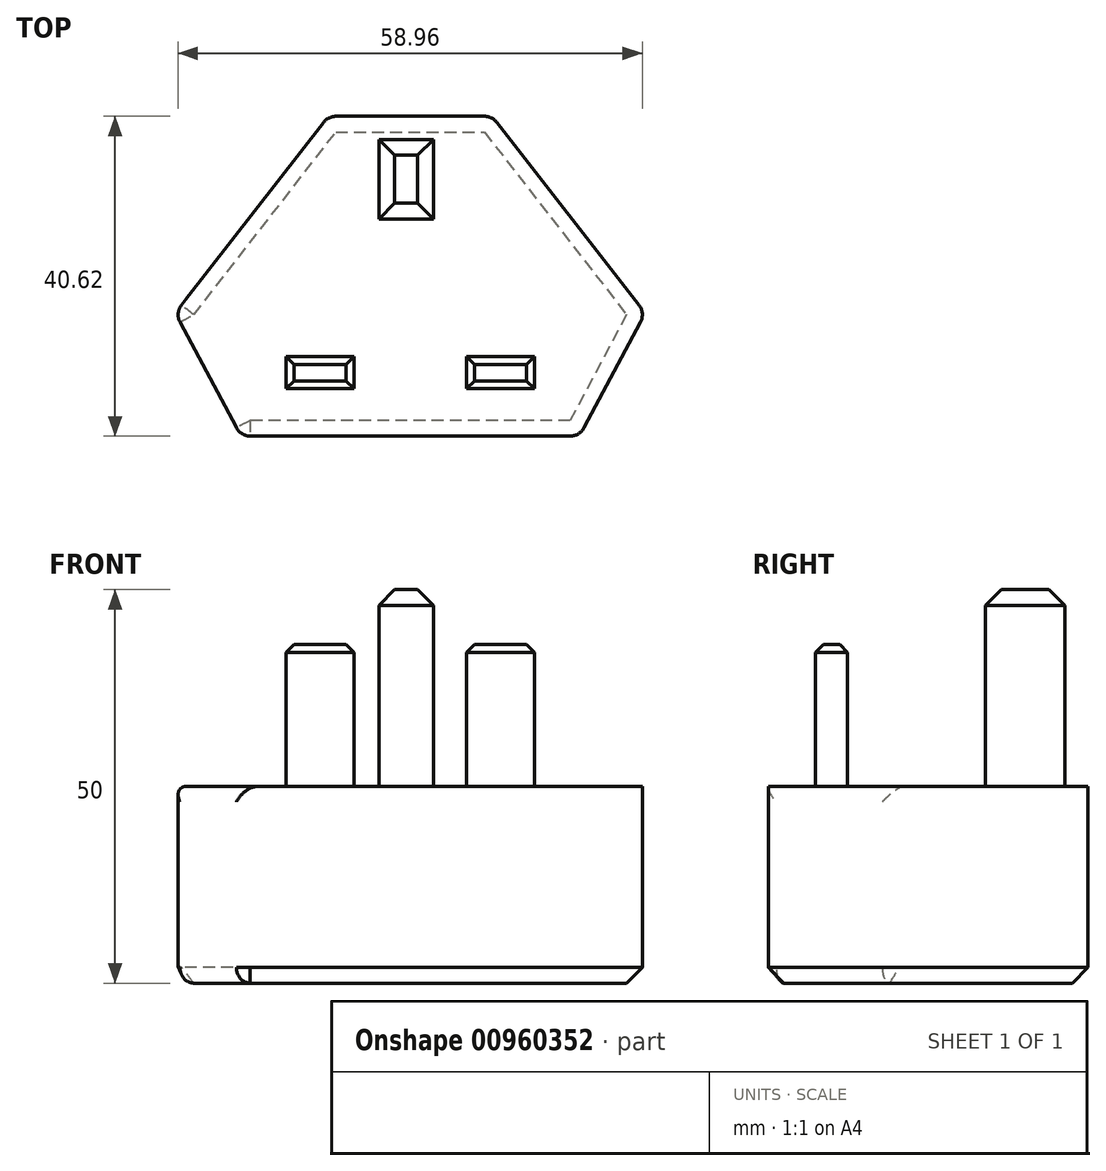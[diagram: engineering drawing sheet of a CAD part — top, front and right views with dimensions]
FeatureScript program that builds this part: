
annotation { "Feature Type Name" : "Feature", "Feature Type Description" : "" }
export const myFeature = defineFeature(function(context is Context, id is Id, definition is map)
    precondition{}
    {
        {
            var Q0;
            Q0=qCreatedBy(makeId("Top.planeOp"),FACE);
            var sketch = newSketch(context, id + "F0", { "sketchPlane" : qUnion([Q0])});
            skLineSegment(sketch, "E0", {"start": v(0, 21.7) * mm, "end": v(10.42, 21.7) * mm});
            skLineSegment(sketch, "E1", {"start": v(10.42, 21.7) * mm, "end": v(29.86, -3.3) * mm});
            skLineSegment(sketch, "E2", {"start": v(29.86, -3.3) * mm, "end": v(21.52, -18.92) * mm});
            skLineSegment(sketch, "E3", {"start": v(21.52, -18.92) * mm, "end": v(0, -18.92) * mm});
            skLineSegment(sketch, "E4", {"start": v(0, 40.44) * mm, "end": v(0, -43.92) * mm, "construction": true});
            skLineSegment(sketch, "E5.MirrorCS", {"start": v(-10.42, 21.7) * mm, "end": v(-29.86, -3.3) * mm});
            skLineSegment(sketch, "E6.MirrorCS", {"start": v(0, 21.7) * mm, "end": v(-10.42, 21.7) * mm});
            skLineSegment(sketch, "E7.MirrorCS", {"start": v(-29.86, -3.3) * mm, "end": v(-21.52, -18.92) * mm});
            skLineSegment(sketch, "E8.MirrorCS", {"start": v(-21.52, -18.92) * mm, "end": v(0, -18.92) * mm});
            skSolve(sketch);
        }
        {
            var Q0;
            Q0 = qSketchRegion(id + "F0", true);
            extrude(context, id + "F1", {"entities" : qUnion([Q0]), "depth" : 25 * mm, "offsetDistance" : 25 * mm});
        }
        {
            var Q0;
            Q0=makeQuery(id+"F1.opExtrude","CAP_FACE",FACE,{"disambiguationData":[OSD([sQuery(id+"F0.wireOp",EDGE,"E0"),sQuery(id+"F0.wireOp",EDGE,"E1"),sQuery(id+"F0.wireOp",EDGE,"E2"),sQuery(id+"F0.wireOp",EDGE,"E3"),sQuery(id+"F0.wireOp",EDGE,"E5.MirrorCS"),sQuery(id+"F0.wireOp",EDGE,"E6.MirrorCS"),sQuery(id+"F0.wireOp",EDGE,"E7.MirrorCS"),sQuery(id+"F0.wireOp",EDGE,"E8.MirrorCS")])],"isStart":false});
            var sketch = newSketch(context, id + "F2", { "sketchPlane" : qUnion([Q0])});
            skLineSegment(sketch, "E9.bottom", {"start": v(-4, 8.68) * mm, "end": v(2.95, 8.68) * mm});
            skLineSegment(sketch, "E9.top", {"start": v(-4, 18.75) * mm, "end": v(2.95, 18.75) * mm});
            skLineSegment(sketch, "E9.left", {"start": v(-4, 8.68) * mm, "end": v(-4, 18.75) * mm});
            skLineSegment(sketch, "E9.right", {"start": v(2.95, 8.68) * mm, "end": v(2.95, 18.75) * mm});
            skLineSegment(sketch, "E10", {"start": v(0, -37.15) * mm, "end": v(0, 72.56) * mm, "construction": true});
            skPoint(sketch, "E10.startSnap0", {"position": v(0, -18.92) * mm});
            skSolve(sketch);
        }
        {
            var Q0;
            Q0=makeQuery(id+"F2.imprint","IMPRINT",FACE,{"disambiguationData":[TD([[makeQuery(id+"F2.imprint","IMPRINT",EDGE,{"derivedFrom":sQuery(id+"F2.wireOp",EDGE,"E9.bottom")}),1.0]])]});
            extrude(context, id + "F3", {"entities" : qUnion([Q0]), "operationType" : NewBodyOperationType.ADD, "depth" : 25 * mm, "offsetDistance" : 25 * mm});
        }
        {
            var Q0;
            Q0=makeQuery(id+"F2.imprint","IMPRINT",FACE,{"disambiguationData":[TD([[makeQuery(id+"F2.imprint","IMPRINT",EDGE,{"derivedFrom":sQuery(id+"F2.wireOp",EDGE,"E9.bottom")}),-1.0]])]});
            var sketch = newSketch(context, id + "F4", { "sketchPlane" : qUnion([Q0])});
            skLineSegment(sketch, "E11.bottom", {"start": v(-15.76, -12.9) * mm, "end": v(-7.15, -12.9) * mm});
            skLineSegment(sketch, "E11.top", {"start": v(-15.76, -8.83) * mm, "end": v(-7.15, -8.83) * mm});
            skLineSegment(sketch, "E11.left", {"start": v(-15.76, -12.9) * mm, "end": v(-15.76, -8.83) * mm});
            skLineSegment(sketch, "E11.right", {"start": v(-7.15, -12.9) * mm, "end": v(-7.15, -8.83) * mm});
            skLineSegment(sketch, "E12.MirrorCS", {"start": v(7.15, -12.9) * mm, "end": v(7.15, -8.83) * mm});
            skLineSegment(sketch, "E13.MirrorCS", {"start": v(15.76, -8.83) * mm, "end": v(7.15, -8.83) * mm});
            skLineSegment(sketch, "E14.MirrorCS", {"start": v(15.76, -12.9) * mm, "end": v(15.76, -8.83) * mm});
            skLineSegment(sketch, "E15.MirrorCS", {"start": v(15.76, -12.9) * mm, "end": v(7.15, -12.9) * mm});
            skSolve(sketch);
        }
        {
            var Q0;
            Q0 = qSketchRegion(id + "F4", true);
            extrude(context, id + "F5", {"entities" : qUnion([Q0]), "operationType" : NewBodyOperationType.ADD, "depth" : 18 * mm, "offsetDistance" : 25 * mm});
        }
        {
            var Q0;
            Q0=makeQuery(id+"F1.opExtrude","SWEPT_EDGE",EDGE,{"disambiguationData":[OSD([sQuery(id+"F0.wireOp",EDGE,"E2"),sQuery(id+"F0.wireOp",EDGE,"E3")])]});
            var Q1;
            Q1=makeQuery(id+"F1.opExtrude","SWEPT_EDGE",EDGE,{"disambiguationData":[OSD([sQuery(id+"F0.wireOp",EDGE,"E7.MirrorCS"),sQuery(id+"F0.wireOp",EDGE,"E8.MirrorCS")])]});
            var Q2;
            Q2=makeQuery(id+"F1.opExtrude","SWEPT_FACE",FACE,{"disambiguationData":[OSD([sQuery(id+"F0.wireOp",EDGE,"E7.MirrorCS")])]});
            var Q3;
            Q3=makeQuery(id+"F1.opExtrude","SWEPT_EDGE",EDGE,{"disambiguationData":[OSD([sQuery(id+"F0.wireOp",EDGE,"E5.MirrorCS"),sQuery(id+"F0.wireOp",EDGE,"E6.MirrorCS")])]});
            var Q4;
            Q4=makeQuery(id+"F1.opExtrude","SWEPT_EDGE",EDGE,{"disambiguationData":[OSD([sQuery(id+"F0.wireOp",EDGE,"E0"),sQuery(id+"F0.wireOp",EDGE,"E1")])]});
            var Q5;
            Q5=makeQuery(id+"F1.opExtrude","SWEPT_EDGE",EDGE,{"disambiguationData":[OSD([sQuery(id+"F0.wireOp",EDGE,"E1"),sQuery(id+"F0.wireOp",EDGE,"E2")])]});
            fillet(context, id + "F6", {"entities" : qUnion([Q0, Q1, Q2, Q3, Q4, Q5]), "radius" : 2 * mm, "tangentPropagation" : true, "allowEdgeOverflow" : false});
        }
        {
            var Q0;
            Q0=makeQuery(id+"F1.opExtrude","CAP_EDGE",EDGE,{"disambiguationData":[OSD([sQuery(id+"F0.wireOp",EDGE,"E0"),sQuery(id+"F0.wireOp",EDGE,"E6.MirrorCS")])],"isStart":true});
            var Q1;
            Q1=makeQuery(id+"F3.opExtrude","CAP_EDGE",EDGE,{"disambiguationData":[OSD([sQuery(id+"F2.wireOp",EDGE,"E9.left")])],"isStart":false});
            var Q2;
            Q2=makeQuery(id+"F3.opExtrude","CAP_EDGE",EDGE,{"disambiguationData":[OSD([sQuery(id+"F2.wireOp",EDGE,"E9.right")])],"isStart":false});
            var Q3;
            Q3=makeQuery(id+"F3.opExtrude","CAP_EDGE",EDGE,{"disambiguationData":[OSD([sQuery(id+"F2.wireOp",EDGE,"E9.top")])],"isStart":false});
            var Q4;
            Q4=makeQuery(id+"F3.opExtrude","CAP_EDGE",EDGE,{"disambiguationData":[OSD([sQuery(id+"F2.wireOp",EDGE,"E9.bottom")])],"isStart":false});
            chamfer(context, id + "F7", {"entities" : qUnion([Q0, Q1, Q2, Q3, Q4]), "width" : 2 * mm, "tangentPropagation" : true});
        }
        {
            var Q0;
            Q0=makeQuery(id+"F5.opExtrude","CAP_EDGE",EDGE,{"disambiguationData":[OSD([sQuery(id+"F4.wireOp",EDGE,"E15.MirrorCS")])],"isStart":false});
            var Q1;
            Q1=makeQuery(id+"F5.opExtrude","CAP_EDGE",EDGE,{"disambiguationData":[OSD([sQuery(id+"F4.wireOp",EDGE,"E13.MirrorCS")])],"isStart":false});
            var Q2;
            Q2=makeQuery(id+"F5.opExtrude","CAP_EDGE",EDGE,{"disambiguationData":[OSD([sQuery(id+"F4.wireOp",EDGE,"E14.MirrorCS")])],"isStart":false});
            var Q3;
            Q3=makeQuery(id+"F5.opExtrude","CAP_EDGE",EDGE,{"disambiguationData":[OSD([sQuery(id+"F4.wireOp",EDGE,"E12.MirrorCS")])],"isStart":false});
            var Q4;
            Q4=makeQuery(id+"F5.opExtrude","CAP_EDGE",EDGE,{"disambiguationData":[OSD([sQuery(id+"F4.wireOp",EDGE,"E11.bottom")])],"isStart":false});
            var Q5;
            Q5=makeQuery(id+"F5.opExtrude","CAP_EDGE",EDGE,{"disambiguationData":[OSD([sQuery(id+"F4.wireOp",EDGE,"E11.top")])],"isStart":false});
            var Q6;
            Q6=makeQuery(id+"F5.opExtrude","CAP_EDGE",EDGE,{"disambiguationData":[OSD([sQuery(id+"F4.wireOp",EDGE,"E11.left")])],"isStart":false});
            var Q7;
            Q7=makeQuery(id+"F5.opExtrude","CAP_EDGE",EDGE,{"disambiguationData":[OSD([sQuery(id+"F4.wireOp",EDGE,"E11.right")])],"isStart":false});
            chamfer(context, id + "F8", {"entities" : qUnion([Q0, Q1, Q2, Q3, Q4, Q5, Q6, Q7]), "width" : 1 * mm, "tangentPropagation" : true});
        }
    });
